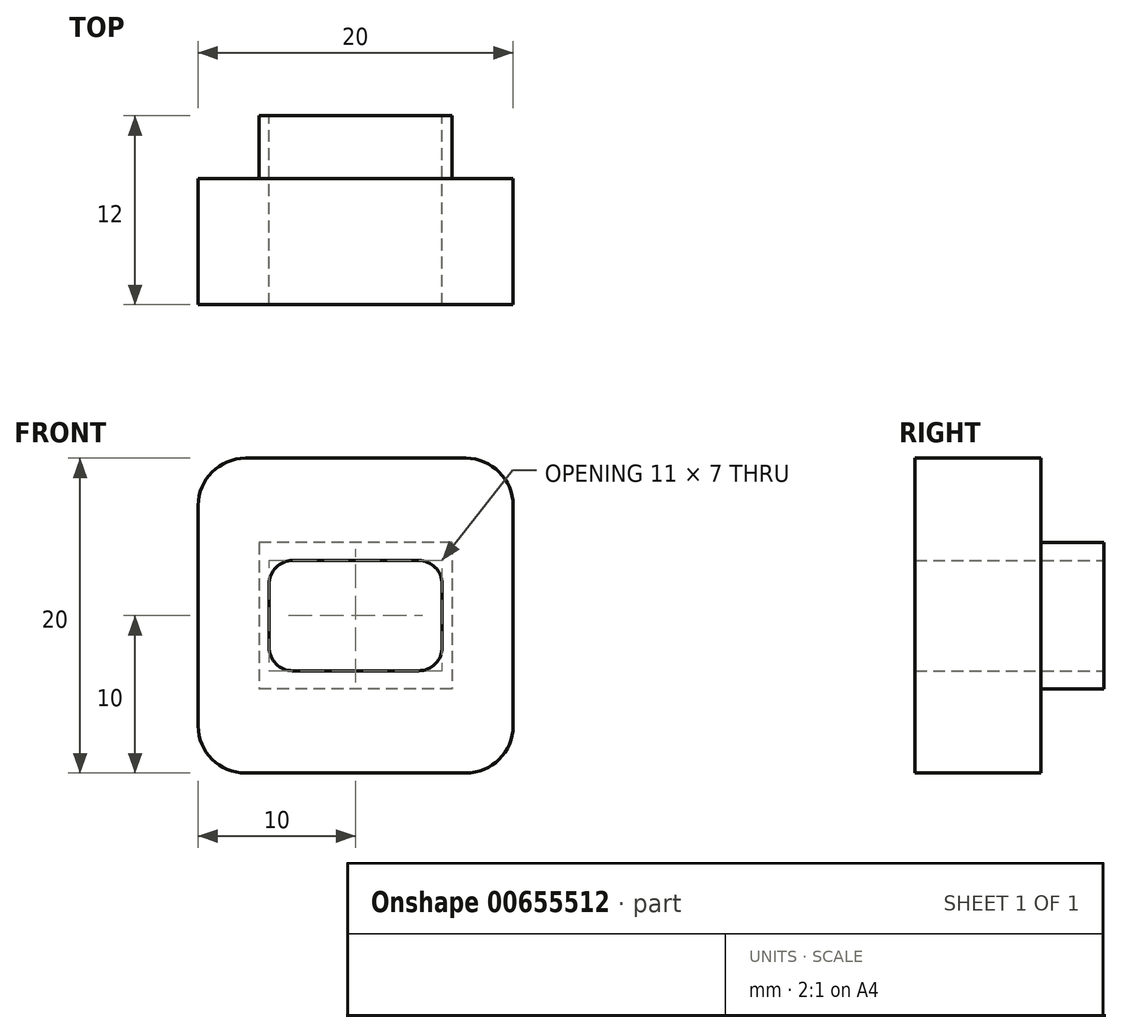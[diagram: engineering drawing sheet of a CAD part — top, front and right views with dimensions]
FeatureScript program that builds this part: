
annotation { "Feature Type Name" : "Feature", "Feature Type Description" : "" }
export const myFeature = defineFeature(function(context is Context, id is Id, definition is map)
    precondition{}
    {
        {
            var Q0;
            Q0=qCreatedBy(makeId("Front.planeOp"),FACE);
            var sketch = newSketch(context, id + "F0", { "sketchPlane" : qUnion([Q0])});
            skLineSegment(sketch, "E0.bottom", {"start": v(7, 10) * mm, "end": v(-7, 10) * mm});
            skLineSegment(sketch, "E0.top", {"start": v(7, -10) * mm, "end": v(-7, -10) * mm});
            skLineSegment(sketch, "E0.left", {"start": v(10, 7) * mm, "end": v(10, -7) * mm});
            skLineSegment(sketch, "E0.right", {"start": v(-10, 7) * mm, "end": v(-10, -7) * mm});
            skPoint(sketch, "E0.middle", {"position": v(0, 0) * mm});
            skPoint(sketch, "E1.visualSharp", {"position": v(10, 10) * mm});
            skArc(sketch, "E1.filletArc", {"start": v(10, 7) * mm, "mid": v(9.12, 9.12) * mm, "end": v(7, 10) * mm});
            skPoint(sketch, "E2.visualSharp", {"position": v(-10, 10) * mm});
            skArc(sketch, "E2.filletArc", {"start": v(-7, 10) * mm, "mid": v(-9.12, 9.12) * mm, "end": v(-10, 7) * mm});
            skPoint(sketch, "E3.visualSharp", {"position": v(-10, -10) * mm});
            skArc(sketch, "E3.filletArc", {"start": v(-10, -7) * mm, "mid": v(-9.12, -9.12) * mm, "end": v(-7, -10) * mm});
            skPoint(sketch, "E4.visualSharp", {"position": v(10, -10) * mm});
            skArc(sketch, "E4.filletArc", {"start": v(7, -10) * mm, "mid": v(9.12, -9.12) * mm, "end": v(10, -7) * mm});
            skSolve(sketch);
        }
        {
            var Q0;
            Q0 = qSketchRegion(id + "F0", true);
            var Q1;
            Q1=makeQuery(id+"F0.imprint","IMPRINT",FACE,{"disambiguationData":[TD([[makeQuery(id+"F0.imprint","IMPRINT",EDGE,{"derivedFrom":sQuery(id+"F0.wireOp",EDGE,"E0.bottom")}),1.0]])]});
            extrude(context, id + "F1", {"entities" : qUnion([Q0, Q1]), "depth" : 8 * mm, "offsetDistance" : 25 * mm});
        }
        {
            var Q0;
            Q0=qCreatedBy(makeId("Front.planeOp"),FACE);
            var sketch = newSketch(context, id + "F2", { "sketchPlane" : qUnion([Q0])});
            skLineSegment(sketch, "E5.bottom", {"start": v(6.12, 4.65) * mm, "end": v(-6.12, 4.65) * mm});
            skLineSegment(sketch, "E5.top", {"start": v(6.12, -4.65) * mm, "end": v(-6.13, -4.65) * mm});
            skLineSegment(sketch, "E5.left", {"start": v(6.12, 4.65) * mm, "end": v(6.12, -4.65) * mm});
            skLineSegment(sketch, "E5.right", {"start": v(-6.12, 4.65) * mm, "end": v(-6.13, -4.65) * mm});
            skPoint(sketch, "E5.middle", {"position": v(0, 0) * mm});
            skSolve(sketch);
        }
        {
            var Q0;
            Q0=makeQuery(id+"F2.imprint","IMPRINT",FACE,{"disambiguationData":[TD([[makeQuery(id+"F2.imprint","IMPRINT",EDGE,{"derivedFrom":sQuery(id+"F2.wireOp",EDGE,"E5.bottom")}),1.0]])]});
            extrude(context, id + "F3", {"entities" : qUnion([Q0]), "operationType" : NewBodyOperationType.ADD, "oppositeDirection" : true, "depth" : 4 * mm, "offsetDistance" : 25 * mm});
        }
        {
            var Q0;
            Q0=makeQuery(id+"F3.opExtrude","CAP_FACE",FACE,{"disambiguationData":[OSD([sQuery(id+"F2.wireOp",EDGE,"E5.bottom"),sQuery(id+"F2.wireOp",EDGE,"E5.top"),sQuery(id+"F2.wireOp",EDGE,"E5.left"),sQuery(id+"F2.wireOp",EDGE,"E5.right")])],"isStart":false});
            var sketch = newSketch(context, id + "F4", { "sketchPlane" : qUnion([Q0])});
            skLineSegment(sketch, "E6.bottom", {"start": v(4, 3.5) * mm, "end": v(-4, 3.5) * mm});
            skLineSegment(sketch, "E6.top", {"start": v(4, -3.5) * mm, "end": v(-4, -3.5) * mm});
            skLineSegment(sketch, "E6.left", {"start": v(5.5, 2) * mm, "end": v(5.5, -2) * mm});
            skLineSegment(sketch, "E6.right", {"start": v(-5.5, 2) * mm, "end": v(-5.5, -2) * mm});
            skPoint(sketch, "E6.middle", {"position": v(0, 0) * mm});
            skPoint(sketch, "E7.visualSharp", {"position": v(-5.5, 3.5) * mm});
            skArc(sketch, "E7.filletArc", {"start": v(-4, 3.5) * mm, "mid": v(-5.06, 3.06) * mm, "end": v(-5.5, 2) * mm});
            skPoint(sketch, "E8.visualSharp", {"position": v(5.5, 3.5) * mm});
            skArc(sketch, "E8.filletArc", {"start": v(5.5, 2) * mm, "mid": v(5.06, 3.06) * mm, "end": v(4, 3.5) * mm});
            skPoint(sketch, "E9.visualSharp", {"position": v(5.5, -3.5) * mm});
            skArc(sketch, "E9.filletArc", {"start": v(4, -3.5) * mm, "mid": v(5.06, -3.06) * mm, "end": v(5.5, -2) * mm});
            skPoint(sketch, "E10.visualSharp", {"position": v(-5.5, -3.5) * mm});
            skArc(sketch, "E10.filletArc", {"start": v(-5.5, -2) * mm, "mid": v(-5.06, -3.06) * mm, "end": v(-4, -3.5) * mm});
            skSolve(sketch);
        }
        {
            var Q0;
            Q0 = qSketchRegion(id + "F4", true);
            extrude(context, id + "F5", {"entities" : qUnion([Q0]), "operationType" : NewBodyOperationType.REMOVE, "oppositeDirection" : true, "depth" : 25 * mm, "offsetDistance" : 25 * mm});
        }
    });
